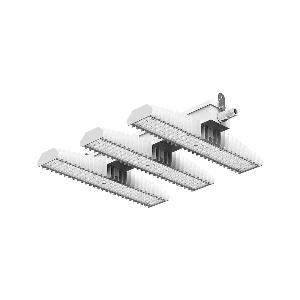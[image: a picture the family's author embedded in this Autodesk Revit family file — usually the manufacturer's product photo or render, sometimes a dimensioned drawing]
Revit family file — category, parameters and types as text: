
# Revit family: 3f_filippi_-_3f_lem_ho_medio_3f_filippi_-_58984_-_3f_lem_3_ho_led_210_dali_cr_medio
name_source: partatom
category: Lighting Fixtures
units: mm (PartAtom-declared; Revit-internal decimal feet)

## family parameters
Cut with Voids When Loaded = No
Host = Face
Light Source = No
Part Type = Normal
Room Calculation Point = No
Round Connector Dimension = Use Diameter
Shared = No

## types (1)
- 3F Filippi - 3F LEM HO Medio (1 x LED, 33192 lm, 207 W, 4000 K)
    Apparent Load = 207 VA
    Approval mark = CE
    CIE Flux Codes = 83 96 99 100 100
    Color Rendering = 80
    Color Temperature = 4000 K
    Control Gear = Electronic transformer
    Default Elevation = 1800 mm
    Description = Industrial luminaire with high light output and high luminous efficiency designed with the most innovative technologies for environments with temperature up to 55°C.

ILLUMINOTECHNICAL
Luminous efficiency 100% (DLOR 100%, ULOR 0%).
Initial luminous flux of the luminaire 33192 lm.
Medium distribution with rectangular shape.
Installation Interdistance Transv.D = 1.02 x hu - Long.D = 1.06 x hu.
Tabular UGR (CIE 117 - 4H-8H; S=0.25H; 70/50/20): RUG 20.2 - 19.8.
Beam angle: 65° - 67°.
Luminous efficacy 160 lm/W.
Lifetime (L93/B10): 30000 h. (tq+25°C)
Lifetime (L90/B10): 50000 h. (tq+25°C)
Lifetime (L85/B10): 80000 h. (tq+25°C)
Lifetime (L80/B10): 100000 h. (tq+25°C)
Lifetime (L85/B10): 50000 h. (tq+55°C)
Sudden decreased luminous flux after 50000 hours: 0% (C0).
Photobiological safety in compliance with IEC/TR 62778: RG0 risk exempt, (IEC 62471).
In compliance with IEC/EN 62722-2-1 - IEC/EN 62717 standards.

SOURCE
3 Mid-Power linear LED modules 70W/840.
Energy efficiency class (UE 2019/2020 - UE 2019/2015): C.
CIE 13.3 Colour rendering index: CRI >80 (R9 <50%).
IES TM-30 Fidelity Index: Rf = 84 Rg = 95.
CCT nominal colour temperature 4000 K.
Colour initial tolerance (MacAdam): SDCM 3.

MECHANICAL
Passive modular heatsinks in die-casted aluminium, painted in white colour.
To optimize the thermal management of the LED module, the heatsinks are oversized and provided with self-cleaning of cooling fins.
Wiring body in aluminium and galvanised steel anchored solidly to the sinks and thermally separated.
3F Lens lenses with high luminous efficiency, transparent methacrylate (PMMA), fixed to the LED modules.
Fixing brackets in stainless steel.
Luminaire with limited surface temperature. - D - (EN 60598-2-24)
Dimensions: 657x542 mm, height 129 mm. Weight 13.375 kg.
IP65 protection degree.
Mechanical strength to impacts IK06 (1 joule).
Glow-wire test resistance 650°C.

ELECTRICAL
Halogen Free DALI-2 DATI (Parts 251, 252, 253), PUSH-DIM, electronic wiring 230V-50/60Hz, power factor 0.97 at full load, THD <25%, constant output current, class I, 2 driver, 2 DALI addresses.
Power of the luminaire 207 W.
ENEC - CE.
SAFE FLICKER: PstLM=<1 and SVM=<0.4 (IEC TR 61547-1 and IEC TR 63158), to ensure a more comfortable and safe light.
Luminaire compliant with EN 60598-2-22 for power supply from a centralised emergency system CPSS (Central Power Supply System), not incorporated in the luminaire - high risk areas excluded. The default power and flux are 100% in AC and 15% in DC.
Ambient temperature from -30°C to +55°C.
Temperature class T6 max 85°C.
Quick connection via M25 5P connector with 9-13 mm tightening range.
Power unit positioned on a separate compartment by the LED module to ensure optimum temperatures of cabling components, to be inspectable and maintainable.
Relative humidity UR: <85%.

INSTALLATION
Ceiling / Suspended / Wall.
All accessories dedicated to this product are available on the Catalog and on our website www.3F-Filippi.com.

APPLICATIONS
In commercial environments, exhibition and industrial areas, stores, open areas.
Environments in which it is necessary a total protection against falling fragments (eg environments with foodstuffs or machines with moving parts or with extreme temperature changes), use luminaires with polycarbonate lenses.

LIGHT MANAGEMENT
Recommended minimum setting: 10%.
The luminaire, equipped with (DALI-2 DATI) driver, can be controlled manually with 3F Easy Dim technology or automatically/manually with wired or wireless DALI/D2D control systems.
The D2D driver guarantees interoperability with other devices with the same certification by making the following information available:
Device Data (Part 251), Energy Report (Part 252), Diagnosis & Maintenance (Part 253).
In electrical systems without a regulation system (manual or automatic) and DALI bus, a suitable jumper must be made on the DA-DA terminals of the appliance.

WARNING
Fixture not suitable for cold stores with an ambient temperature <0°C and/or relative humidity >85%.
Luminaire designed for disposal/recycling at end-of-life.
Replaceable (LED only) light source by a professional. Replaceable control gear by a professional.
    Height = 129 mm
    Lamp = 1 x LED
    Lamp Light Flux = 33192 lm
    Lamp Power = 207 W
    Lamp count = 1
    Length = 657 mm
    Lifetime = 50000 h
    Luminous efficacy = 160 lm/W
    Manufacturer = 3F Filippi
    ModVariant = No
    Model = 3F Filippi - 58984 - 3F LEM 3 HO LED 210 DALI CR MEDIO
    Mounting Place = Ceiling
    Mounting Type = Pendant
    Number of Poles = 1
    OnlyDefault = Yes
    Power Factor = 1
    Product Name = 3F Filippi - 3F LEM HO Medio
    Product group = pendant luminaire
    ProductGroupID = 9
    Protection Class = Protection class I
    Protection Degree = IP 65
    RLX_Detail_Level = 1
    RLX_Emergency_Light_Flux = 0 lm
    RLX_Emergency_Type = 0
    RLX_Emergency_Type_DB = No
    RlxData = <blob elided: 102697 chars, md5=5c306782>
    Socket = socket
    Standby Power = 0 W
    System Light Flux = 33192 lm
    System Power = 207 W
    Type Comments = Product without accessories
    Type Image = 3f_filippi_-_lem_3.jpg
    URL = http://relux.com
    VarID = ---
    Voltage = 0 V
    Weight = 0.00 kg
    Width = 542 mm

## geometry (parser evidence)
native form markers: Blend x4, Sweep x12
no freeform markers — native parametric forms only
